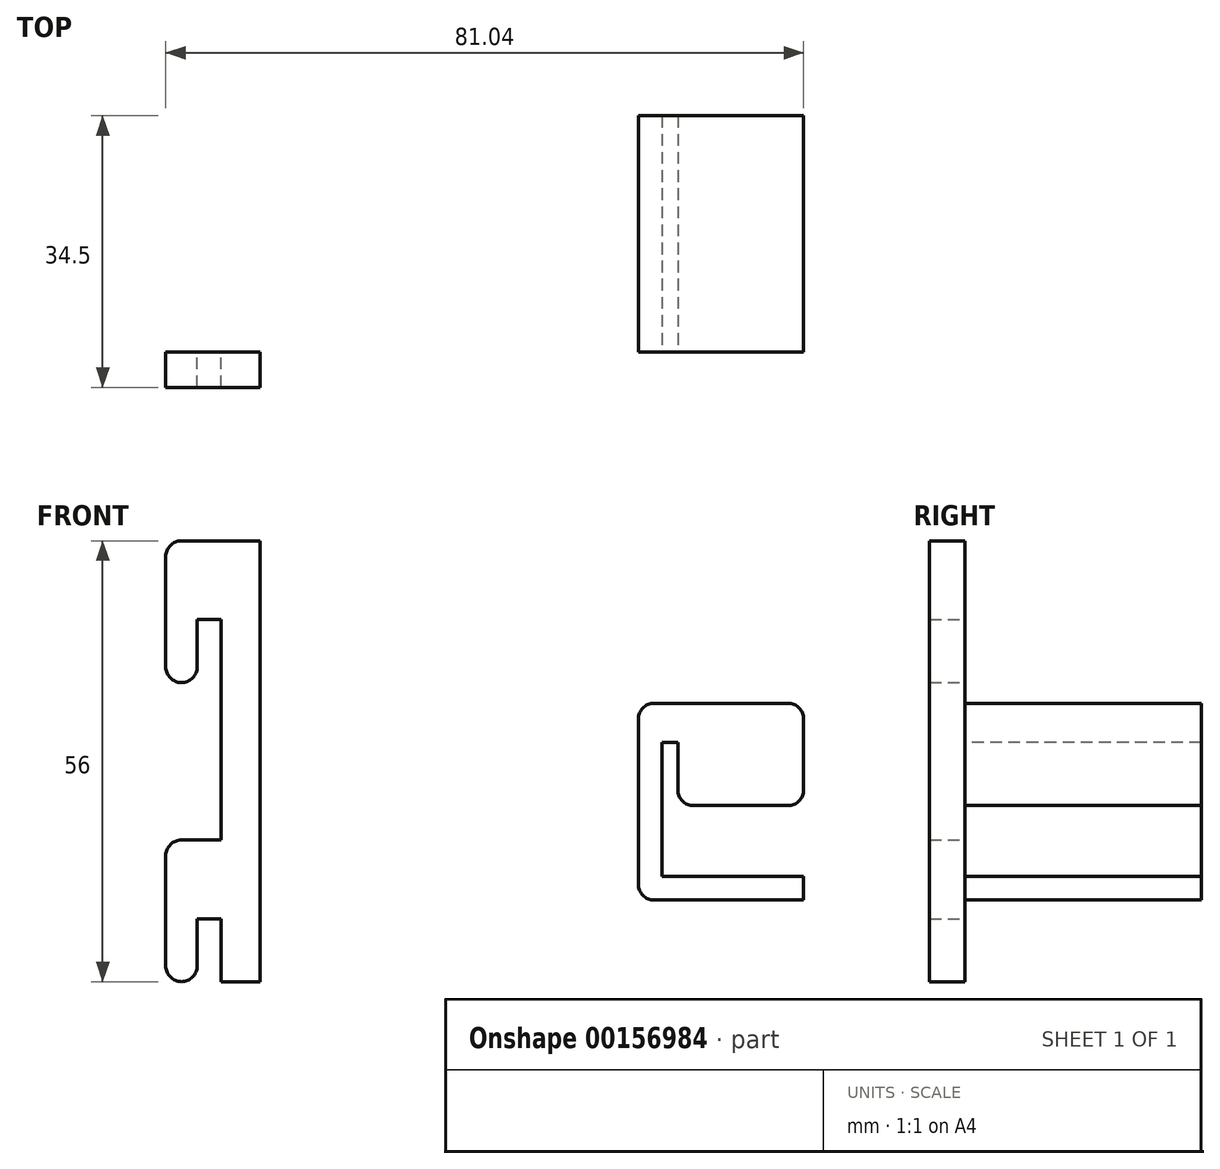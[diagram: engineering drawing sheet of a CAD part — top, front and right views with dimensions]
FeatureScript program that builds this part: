
annotation { "Feature Type Name" : "Feature", "Feature Type Description" : "" }
export const myFeature = defineFeature(function(context is Context, id is Id, definition is map)
    precondition{}
    {
        {
            var Q0;
            Q0=qCreatedBy(makeId("Front.planeOp"),FACE);
            var sketch = newSketch(context, id + "F0", { "sketchPlane" : qUnion([Q0])});
            skLineSegment(sketch, "E0", {"start": v(21, 12) * mm, "end": v(21, 25) * mm});
            skLineSegment(sketch, "E1", {"start": v(21, 25) * mm, "end": v(0, 25) * mm});
            skLineSegment(sketch, "E2", {"start": v(0, 25) * mm, "end": v(0, 0) * mm});
            skLineSegment(sketch, "E3", {"start": v(0, 0) * mm, "end": v(21, 0) * mm});
            skLineSegment(sketch, "E4", {"start": v(21, 0) * mm, "end": v(21, 3) * mm});
            skLineSegment(sketch, "E5", {"start": v(21, 3) * mm, "end": v(3, 3) * mm});
            skLineSegment(sketch, "E6", {"start": v(3, 3) * mm, "end": v(3, 20) * mm});
            skLineSegment(sketch, "E7", {"start": v(3, 20) * mm, "end": v(5, 20) * mm});
            skLineSegment(sketch, "E8.right", {"start": v(5, 20) * mm, "end": v(5, 12) * mm});
            skLineSegment(sketch, "E9", {"start": v(21, 12) * mm, "end": v(5, 12) * mm});
            skSolve(sketch);
        }
        {
            var Q0;
            Q0 = qSketchRegion(id + "F0", true);
            extrude(context, id + "F1", {"entities" : qUnion([Q0]), "oppositeDirection" : true, "depth" : 30 * mm});
        }
        {
            var Q0;
            Q0=makeQuery(id+"F1.opExtrude","SWEPT_EDGE",EDGE,{"disambiguationData":[OSD([sQuery(id+"F0.wireOp",EDGE,"E0"),sQuery(id+"F0.wireOp",EDGE,"E1")])]});
            var Q1;
            Q1=makeQuery(id+"F1.opExtrude","SWEPT_EDGE",EDGE,{"disambiguationData":[OSD([sQuery(id+"F0.wireOp",EDGE,"E1"),sQuery(id+"F0.wireOp",EDGE,"E2")])]});
            var Q2;
            Q2=makeQuery(id+"F1.opExtrude","SWEPT_EDGE",EDGE,{"disambiguationData":[OSD([sQuery(id+"F0.wireOp",EDGE,"E0"),sQuery(id+"F0.wireOp",EDGE,"E9")])]});
            var Q3;
            Q3=makeQuery(id+"F1.opExtrude","SWEPT_EDGE",EDGE,{"disambiguationData":[OSD([sQuery(id+"F0.wireOp",EDGE,"E2"),sQuery(id+"F0.wireOp",EDGE,"E3")])]});
            var Q4;
            Q4=makeQuery(id+"F1.opExtrude","SWEPT_EDGE",EDGE,{"disambiguationData":[OSD([sQuery(id+"F0.wireOp",EDGE,"E8.right"),sQuery(id+"F0.wireOp",EDGE,"E9")])]});
            fillet(context, id + "F2", {"entities" : qUnion([Q0, Q1, Q2, Q3, Q4]), "radius" : 2 * mm, "tangentPropagation" : true, "allowEdgeOverflow" : false});
        }
        {
            var Q0;
            Q0=qCreatedBy(makeId("Front.planeOp"),FACE);
            var sketch = newSketch(context, id + "F3", { "sketchPlane" : qUnion([Q0])});
            skLineSegment(sketch, "E10.bottom", {"start": v(-60.04, 45.63) * mm, "end": v(-56.04, 45.63) * mm});
            skLineSegment(sketch, "E10.top", {"start": v(-60.04, 27.63) * mm, "end": v(-56.04, 27.63) * mm});
            skLineSegment(sketch, "E10.left", {"start": v(-60.04, 45.63) * mm, "end": v(-60.04, 27.63) * mm});
            skLineSegment(sketch, "E10.right", {"start": v(-56.04, 45.63) * mm, "end": v(-56.04, 27.63) * mm});
            skLineSegment(sketch, "E11.bottom", {"start": v(-56.04, 45.63) * mm, "end": v(-53.04, 45.63) * mm});
            skLineSegment(sketch, "E11.top", {"start": v(-56.04, 35.63) * mm, "end": v(-53.04, 35.63) * mm});
            skLineSegment(sketch, "E11.left", {"start": v(-56.04, 45.63) * mm, "end": v(-56.04, 35.63) * mm});
            skLineSegment(sketch, "E11.right", {"start": v(-53.04, 45.63) * mm, "end": v(-53.04, 35.63) * mm});
            skLineSegment(sketch, "E12.bottom", {"start": v(-60.04, 7.63) * mm, "end": v(-56.04, 7.63) * mm});
            skLineSegment(sketch, "E12.top", {"start": v(-60.04, -10.37) * mm, "end": v(-56.04, -10.37) * mm});
            skLineSegment(sketch, "E12.left", {"start": v(-60.04, 7.63) * mm, "end": v(-60.04, -10.37) * mm});
            skLineSegment(sketch, "E12.right", {"start": v(-56.04, 7.63) * mm, "end": v(-56.04, -10.37) * mm});
            skLineSegment(sketch, "E13.bottom", {"start": v(-56.04, 7.63) * mm, "end": v(-53.04, 7.63) * mm});
            skLineSegment(sketch, "E13.top", {"start": v(-56.04, -2.37) * mm, "end": v(-53.04, -2.37) * mm});
            skLineSegment(sketch, "E13.left", {"start": v(-56.04, 7.63) * mm, "end": v(-56.04, -2.37) * mm});
            skLineSegment(sketch, "E13.right", {"start": v(-53.04, 7.63) * mm, "end": v(-53.04, -2.37) * mm});
            skLineSegment(sketch, "E14.bottom", {"start": v(-53.04, 45.63) * mm, "end": v(-48.04, 45.63) * mm});
            skLineSegment(sketch, "E14.top", {"start": v(-53.04, -10.37) * mm, "end": v(-48.04, -10.37) * mm});
            skLineSegment(sketch, "E14.left", {"start": v(-53.04, 45.63) * mm, "end": v(-53.04, -10.37) * mm});
            skLineSegment(sketch, "E14.right", {"start": v(-48.04, 45.63) * mm, "end": v(-48.04, -10.37) * mm});
            skSolve(sketch);
        }
        {
            var Q0;
            Q0 = qSketchRegion(id + "F3", true);
            extrude(context, id + "F4", {"entities" : qUnion([Q0]), "depth" : 4.5 * mm});
        }
        {
            var Q0;
            Q0=makeQuery(id+"F4.opExtrude","CAP_FACE",FACE,{"disambiguationData":[OSD([sQuery(id+"F3.wireOp",EDGE,"E10.bottom"),sQuery(id+"F3.wireOp",EDGE,"E10.top"),sQuery(id+"F3.wireOp",EDGE,"E10.left"),sQuery(id+"F3.wireOp",EDGE,"E10.right"),sQuery(id+"F3.wireOp",EDGE,"E11.bottom"),sQuery(id+"F3.wireOp",EDGE,"E11.top"),sQuery(id+"F3.wireOp",EDGE,"E12.bottom"),sQuery(id+"F3.wireOp",EDGE,"E12.top"),sQuery(id+"F3.wireOp",EDGE,"E12.left"),sQuery(id+"F3.wireOp",EDGE,"E12.right"),sQuery(id+"F3.wireOp",EDGE,"E13.bottom"),sQuery(id+"F3.wireOp",EDGE,"E13.top"),sQuery(id+"F3.wireOp",EDGE,"E14.bottom"),sQuery(id+"F3.wireOp",EDGE,"E14.top"),sQuery(id+"F3.wireOp",EDGE,"E14.left"),sQuery(id+"F3.wireOp",EDGE,"E14.right")])],"isStart":false});
            var sketch = newSketch(context, id + "F5", { "sketchPlane" : qUnion([Q0])});
            skLineSegment(sketch, "E15.bottom", {"start": v(-48.04, 45.63) * mm, "end": v(-53.04, 45.63) * mm});
            skLineSegment(sketch, "E15.top", {"start": v(-48.04, -10.37) * mm, "end": v(-53.04, -10.37) * mm});
            skLineSegment(sketch, "E15.left", {"start": v(-48.04, 45.63) * mm, "end": v(-48.04, -10.37) * mm});
            skLineSegment(sketch, "E15.right", {"start": v(-53.04, 45.63) * mm, "end": v(-53.04, -10.37) * mm});
            skSolve(sketch);
        }
        {
            var Q0;
            Q0=makeQuery(id+"F4.opExtrude","SWEPT_EDGE",EDGE,{"disambiguationData":[OSD([sQuery(id+"F3.wireOp",EDGE,"E12.top"),sQuery(id+"F3.wireOp",EDGE,"E12.right")])]});
            var Q1;
            Q1=makeQuery(id+"F4.opExtrude","SWEPT_EDGE",EDGE,{"disambiguationData":[OSD([sQuery(id+"F3.wireOp",EDGE,"E12.top"),sQuery(id+"F3.wireOp",EDGE,"E12.left")])]});
            var Q2;
            Q2=makeQuery(id+"F4.opExtrude","SWEPT_EDGE",EDGE,{"disambiguationData":[OSD([sQuery(id+"F3.wireOp",EDGE,"E12.bottom"),sQuery(id+"F3.wireOp",EDGE,"E12.left")])]});
            var Q3;
            Q3=makeQuery(id+"F4.opExtrude","SWEPT_EDGE",EDGE,{"disambiguationData":[OSD([sQuery(id+"F3.wireOp",EDGE,"E10.top"),sQuery(id+"F3.wireOp",EDGE,"E10.left")])]});
            var Q4;
            Q4=makeQuery(id+"F4.opExtrude","SWEPT_EDGE",EDGE,{"disambiguationData":[OSD([sQuery(id+"F3.wireOp",EDGE,"E10.top"),sQuery(id+"F3.wireOp",EDGE,"E10.right")])]});
            var Q5;
            Q5=makeQuery(id+"F4.opExtrude","SWEPT_EDGE",EDGE,{"disambiguationData":[OSD([sQuery(id+"F3.wireOp",EDGE,"E10.bottom"),sQuery(id+"F3.wireOp",EDGE,"E10.left")])]});
            fillet(context, id + "F6", {"entities" : qUnion([Q0, Q1, Q2, Q3, Q4, Q5]), "radius" : 2 * mm, "tangentPropagation" : true, "allowEdgeOverflow" : false});
        }
    });
